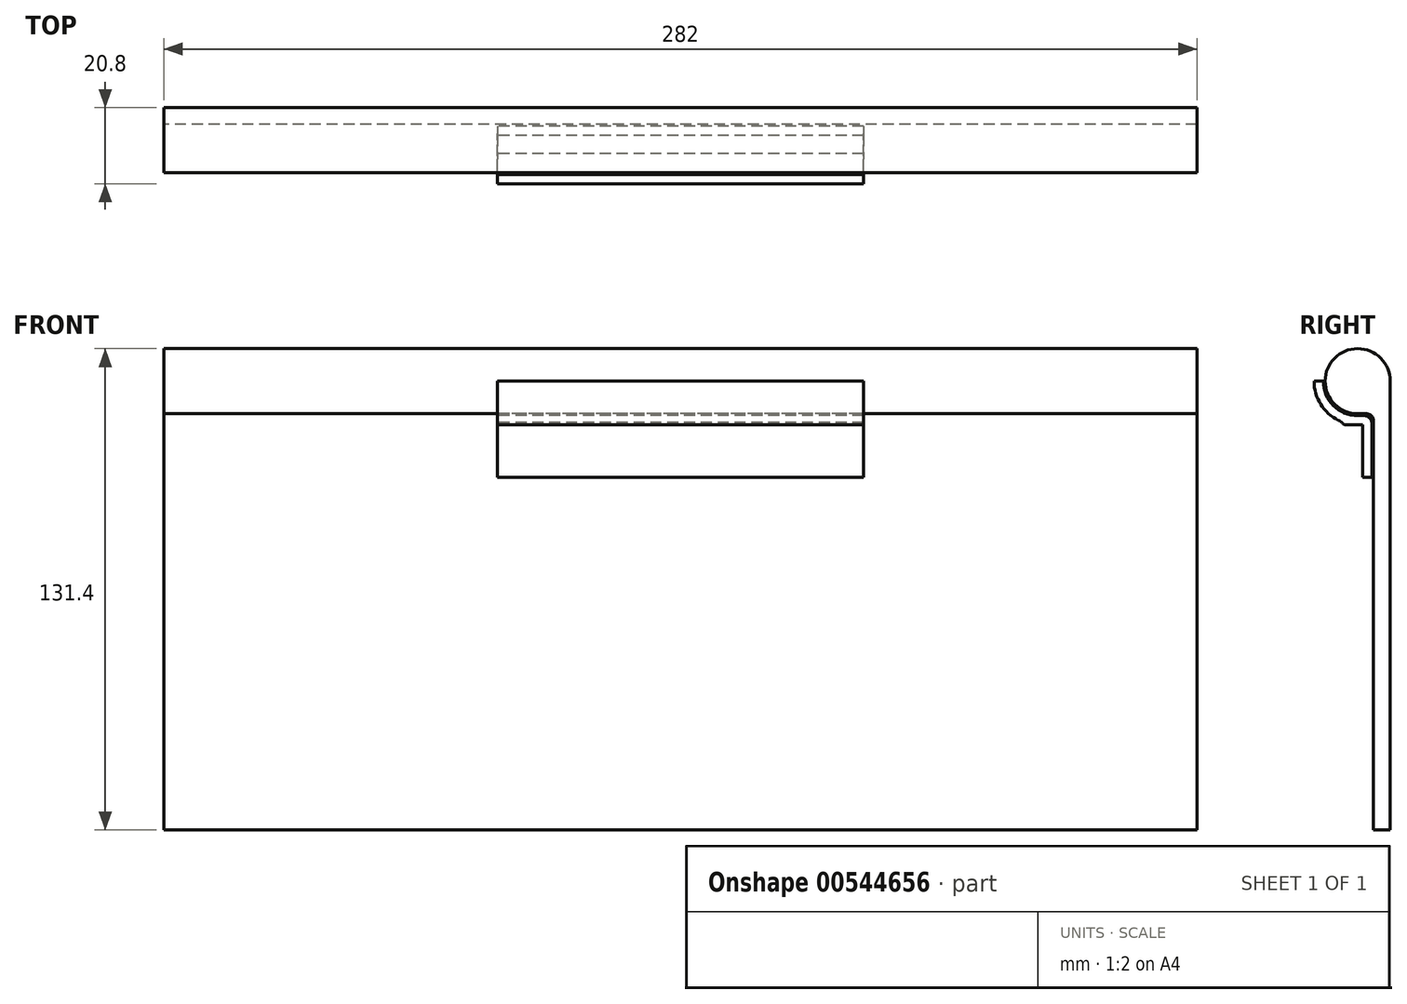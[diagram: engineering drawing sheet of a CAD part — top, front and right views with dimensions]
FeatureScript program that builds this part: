
annotation { "Feature Type Name" : "Feature", "Feature Type Description" : "" }
export const myFeature = defineFeature(function(context is Context, id is Id, definition is map)
    precondition{}
    {
        {
            var Q0;
            Q0=qCreatedBy(makeId("Right.planeOp"),FACE);
            var sketch = newSketch(context, id + "F0", { "sketchPlane" : qUnion([Q0])});
            skCircle(sketch, "E0", {"center": v(0, 0) * mm, "radius": 8.9 * mm});
            skLineSegment(sketch, "E1.bottom", {"start": v(4.35, 8.9) * mm, "end": v(0, 8.9) * mm, "construction": true});
            skLineSegment(sketch, "E1.top", {"start": v(8.9, -122.5) * mm, "end": v(4.35, -122.5) * mm});
            skLineSegment(sketch, "E1.left", {"start": v(8.9, 0) * mm, "end": v(8.9, -122.5) * mm});
            skLineSegment(sketch, "E1.right", {"start": v(4.35, -10.9) * mm, "end": v(4.35, -122.5) * mm});
            skLineSegment(sketch, "E2", {"start": v(0, -8.9) * mm, "end": v(2.35, -8.9) * mm});
            skArc(sketch, "E3.filletArc", {"start": v(4.35, -10.9) * mm, "mid": v(3.76, -9.49) * mm, "end": v(2.35, -8.9) * mm});
            skSolve(sketch);
        }
        {
            var Q0;
            Q0 = qSketchRegion(id + "F0", true);
            extrude(context, id + "F1", {"entities" : qUnion([Q0]), "endBound" : BoundingType.SYMMETRIC, "depth" : 282 * mm, "offsetDistance" : 25 * mm});
        }
        {
            var Q0;
            Q0=qCreatedBy(makeId("Right.planeOp"),FACE);
            var sketch = newSketch(context, id + "F2", { "sketchPlane" : qUnion([Q0])});
            skArc(sketch, "E4.0", {"start": v(-9.4, 0) * mm, "mid": v(-6.65, -6.65) * mm, "end": v(0, -9.4) * mm});
            skLineSegment(sketch, "E5.0", {"start": v(3.85, -11.26) * mm, "end": v(3.85, -26.26) * mm});
            skArc(sketch, "E6", {"start": v(-11.9, 0) * mm, "mid": v(-6.92, -9.68) * mm, "end": v(3.85, -11.26) * mm});
            skLineSegment(sketch, "E7", {"start": v(3.85, -11.4) * mm, "end": v(3.85, -11.26) * mm});
            skLineSegment(sketch, "E8", {"start": v(0, -9.4) * mm, "end": v(1.85, -9.4) * mm});
            skPoint(sketch, "E9.newPointB", {"position": v(3.85, -9.4) * mm});
            skArc(sketch, "E9.filletArc", {"start": v(3.85, -11.4) * mm, "mid": v(3.26, -9.99) * mm, "end": v(1.85, -9.4) * mm});
            skLineSegment(sketch, "E10", {"start": v(-11.9, 0) * mm, "end": v(-9.4, 0) * mm});
            skLineSegment(sketch, "E11.top", {"start": v(3.85, -26.26) * mm, "end": v(1.35, -26.26) * mm});
            skLineSegment(sketch, "E11.right", {"start": v(1.35, -11.82) * mm, "end": v(1.35, -26.26) * mm});
            skLineSegment(sketch, "E12", {"start": v(1.35, -11.9) * mm, "end": v(-3.65, -11.9) * mm});
            skLineSegment(sketch, "E13", {"start": v(-3.65, -11.9) * mm, "end": v(-3.65, -11.33) * mm});
            skSolve(sketch);
        }
        {
            var Q0;
            Q0 = qSketchRegion(id + "F2", true);
            extrude(context, id + "F3", {"entities" : qUnion([Q0]), "endBound" : BoundingType.SYMMETRIC, "depth" : 100 * mm, "offsetDistance" : 25 * mm});
        }
        {
            var Q0;
            Q0=makeQuery(id+"F3.opExtrude","SWEPT_EDGE",EDGE,{"disambiguationData":[OSD([sQuery(id+"F2.wireOp",EDGE,"E6"),sQuery(id+"F2.wireOp",EDGE,"E13")])]});
            fillet(context, id + "F4", {"entities" : qUnion([Q0]), "radius" : 5 * mm, "tangentPropagation" : true, "allowEdgeOverflow" : false});
        }
    });
